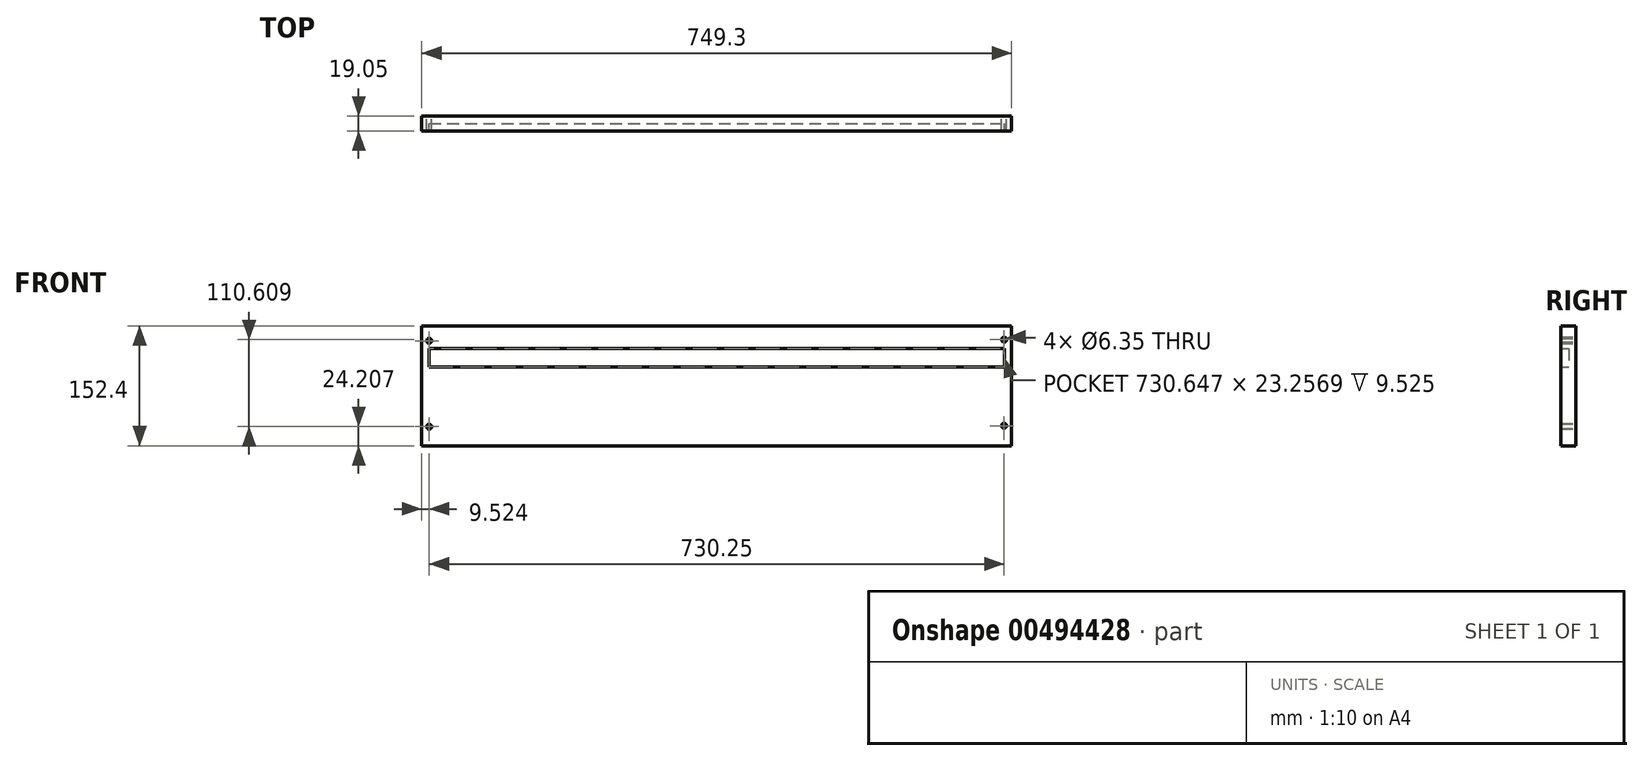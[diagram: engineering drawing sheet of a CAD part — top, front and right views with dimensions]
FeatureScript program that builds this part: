
annotation { "Feature Type Name" : "Feature", "Feature Type Description" : "" }
export const myFeature = defineFeature(function(context is Context, id is Id, definition is map)
    precondition{}
    {
        {
            var Q0;
            Q0=qCreatedBy(makeId("Front.planeOp"),FACE);
            var sketch = newSketch(context, id + "F0", { "sketchPlane" : qUnion([Q0])});
            skLineSegment(sketch, "E0", {"start": v(-218.5, 54.24) * mm, "end": v(-218.5, -98.16) * mm});
            skLineSegment(sketch, "E1", {"start": v(-218.5, -98.16) * mm, "end": v(-199.44, -98.16) * mm});
            skLineSegment(sketch, "E2", {"start": v(-218.5, 54.24) * mm, "end": v(-199.44, 54.24) * mm});
            skLineSegment(sketch, "E3", {"start": v(156.16, -191.31) * mm, "end": v(156.16, 212.37) * mm, "construction": true});
            skLineSegment(sketch, "E4.MirrorCS", {"start": v(530.8, 54.24) * mm, "end": v(530.8, -98.16) * mm});
            skLineSegment(sketch, "E5.MirrorCS", {"start": v(530.8, 54.24) * mm, "end": v(511.76, 54.24) * mm});
            skLineSegment(sketch, "E6.MirrorCS", {"start": v(530.8, -98.16) * mm, "end": v(511.76, -98.16) * mm});
            skPoint(sketch, "E7.visualSharp", {"position": v(156.16, -11.1) * mm});
            skLineSegment(sketch, "E8", {"start": v(-199.44, 54.24) * mm, "end": v(511.76, 54.24) * mm});
            skLineSegment(sketch, "E9", {"start": v(511.76, -98.16) * mm, "end": v(-199.44, -98.16) * mm});
            skCircle(sketch, "E10", {"center": v(-208.97, 35.19) * mm, "radius": 3.18 * mm});
            skCircle(sketch, "E11.MirrorC", {"center": v(521.28, 36.66) * mm, "radius": 3.18 * mm});
            skCircle(sketch, "E12.MirrorC", {"center": v(-208.97, -73.95) * mm, "radius": 3.18 * mm});
            skCircle(sketch, "E13.MirrorC", {"center": v(521.28, -72.72) * mm, "radius": 3.18 * mm});
            skLineSegment(sketch, "E14", {"start": v(-209.16, 13.55) * mm, "end": v(521.48, 13.55) * mm, "construction": true});
            skLineSegment(sketch, "E15", {"start": v(-209.16, 13.55) * mm, "end": v(-209.16, 25.18) * mm});
            skLineSegment(sketch, "E16", {"start": v(521.48, 13.55) * mm, "end": v(521.48, 25.18) * mm});
            skLineSegment(sketch, "E17.MirrorCS", {"start": v(-218.5, 1.92) * mm, "end": v(530.8, 1.92) * mm});
            skLineSegment(sketch, "E18.MirrorCS", {"start": v(521.48, 13.55) * mm, "end": v(521.48, 1.92) * mm});
            skLineSegment(sketch, "E19.MirrorCS", {"start": v(-209.16, 13.55) * mm, "end": v(-209.16, 1.92) * mm});
            skLineSegment(sketch, "E20", {"start": v(-209.16, 25.18) * mm, "end": v(521.48, 25.18) * mm});
            skSolve(sketch);
        }
        {
            var Q0;
            Q0 = qSketchRegion(id + "F0", true);
            extrude(context, id + "F1", {"entities" : qUnion([Q0]), "depth" : 19.05 * mm, "offsetDistance" : 25.4 * mm});
        }
        {
            var Q0;
            Q0=makeQuery(id+"F0.imprint","IMPRINT",FACE,{"disambiguationData":[TD([[makeQuery(id+"F0.imprint","IMPRINT",EDGE,{"derivedFrom":sQuery(id+"F0.wireOp",EDGE,"E15")}),-1.0]])]});
            extrude(context, id + "F2", {"entities" : qUnion([Q0]), "operationType" : NewBodyOperationType.ADD, "depth" : 9.52 * mm, "offsetDistance" : 25.4 * mm});
        }
    });
